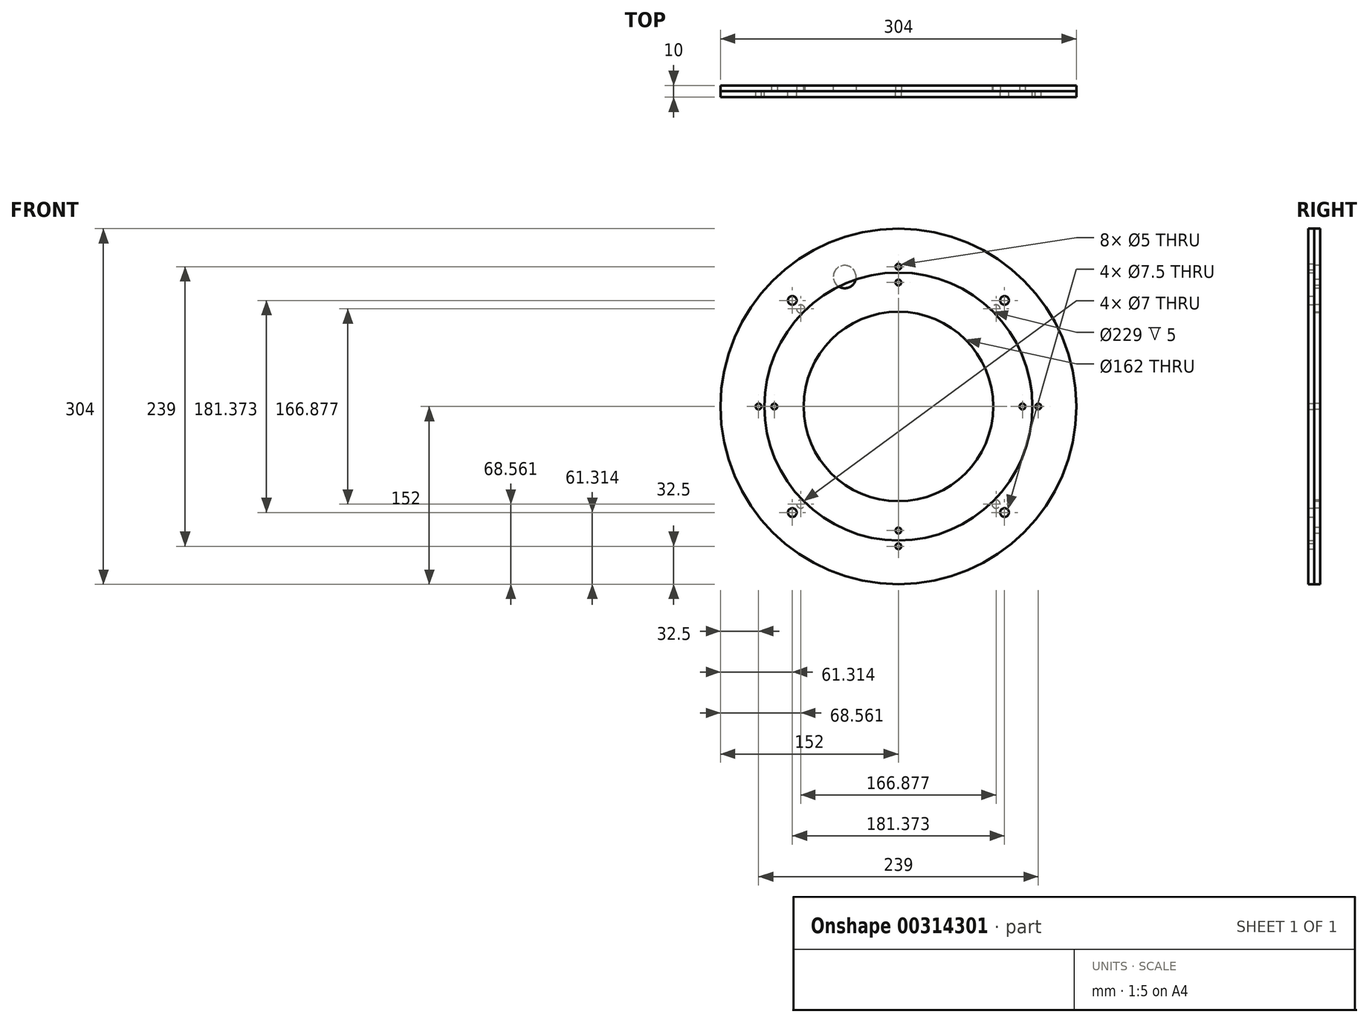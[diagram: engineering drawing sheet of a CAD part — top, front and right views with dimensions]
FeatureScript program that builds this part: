
annotation { "Feature Type Name" : "Feature", "Feature Type Description" : "" }
export const myFeature = defineFeature(function(context is Context, id is Id, definition is map)
    precondition{}
    {
        {
            var Q0;
            Q0=qCreatedBy(makeId("Front.planeOp"),FACE);
            var sketch = newSketch(context, id + "F0", { "sketchPlane" : qUnion([Q0])});
            skCircle(sketch, "E0", {"center": v(0, 0) * mm, "radius": 152 * mm});
            skCircle(sketch, "E1", {"center": v(0, 0) * mm, "radius": 81 * mm});
            skSolve(sketch);
        }
        {
            var Q0;
            Q0=makeQuery(id+"F0.imprint","IMPRINT",FACE,{"disambiguationData":[TD([[makeQuery(id+"F0.imprint","IMPRINT",EDGE,{"derivedFrom":sQuery(id+"F0.wireOp",EDGE,"E0")}),1.0]])]});
            extrude(context, id + "F1", {"entities" : qUnion([Q0]), "depth" : 5 * mm});
        }
        {
            var Q0;
            Q0=makeQuery(id+"F1.opExtrude","CAP_FACE",FACE,{"disambiguationData":[OSD([sQuery(id+"F0.wireOp",EDGE,"E0"),sQuery(id+"F0.wireOp",EDGE,"E1")])],"isStart":false});
            var sketch = newSketch(context, id + "F2", { "sketchPlane" : qUnion([Q0])});
            skCircle(sketch, "E2", {"center": v(0, 0) * mm, "radius": 106 * mm, "construction": true});
            skLineSegment(sketch, "E3", {"start": v(0, 0) * mm, "end": v(0, 106) * mm, "construction": true});
            skLineSegment(sketch, "E4", {"start": v(0, 0) * mm, "end": v(-106, 0) * mm, "construction": true});
            skLineSegment(sketch, "E5", {"start": v(0, 0) * mm, "end": v(0, -106) * mm, "construction": true});
            skLineSegment(sketch, "E6", {"start": v(0, 0) * mm, "end": v(106, 0) * mm, "construction": true});
            skCircle(sketch, "E7", {"center": v(0, 106) * mm, "radius": 2.5 * mm});
            skCircle(sketch, "E8", {"center": v(-106, 0) * mm, "radius": 2.5 * mm});
            skCircle(sketch, "E9", {"center": v(0, -106) * mm, "radius": 2.5 * mm});
            skCircle(sketch, "E10", {"center": v(106, 0) * mm, "radius": 2.5 * mm});
            skSolve(sketch);
        }
        {
            var Q0;
            Q0=makeQuery(id+"F2.imprint","IMPRINT",FACE,{"disambiguationData":[TD([[makeQuery(id+"F2.imprint","IMPRINT",EDGE,{"derivedFrom":sQuery(id+"F2.wireOp",EDGE,"E7")}),1.0]])]});
            extrude(context, id + "F3", {"entities" : qUnion([Q0]), "operationType" : NewBodyOperationType.REMOVE, "oppositeDirection" : true, "depth" : 5 * mm});
        }
        {
            var Q0;
            Q0=makeQuery(id+"F1.opExtrude","CAP_FACE",FACE,{"disambiguationData":[OSD([sQuery(id+"F0.wireOp",EDGE,"E0"),sQuery(id+"F0.wireOp",EDGE,"E1")])],"isStart":false});
            var sketch = newSketch(context, id + "F4", { "sketchPlane" : qUnion([Q0])});
            skSolve(sketch);
        }
        {
            var Q0;
            Q0 = qSketchRegion(id + "F4", true);
            var Q1;
            Q1=makeQuery(id+"F2.imprint","IMPRINT",FACE,{"disambiguationData":[TD([[makeQuery(id+"F2.imprint","IMPRINT",EDGE,{"derivedFrom":sQuery(id+"F2.wireOp",EDGE,"E8")}),1.0]])]});
            extrude(context, id + "F5", {"entities" : qUnion([Q0, Q1]), "operationType" : NewBodyOperationType.REMOVE, "oppositeDirection" : true, "depth" : 5 * mm});
        }
        {
            var Q0;
            Q0=makeQuery(id+"F2.imprint","IMPRINT",FACE,{"disambiguationData":[TD([[makeQuery(id+"F2.imprint","IMPRINT",EDGE,{"derivedFrom":sQuery(id+"F2.wireOp",EDGE,"E9")}),1.0]])]});
            extrude(context, id + "F6", {"entities" : qUnion([Q0]), "operationType" : NewBodyOperationType.REMOVE, "oppositeDirection" : true, "depth" : 5 * mm});
        }
        {
            var Q0;
            Q0=makeQuery(id+"F2.imprint","IMPRINT",FACE,{"disambiguationData":[TD([[makeQuery(id+"F2.imprint","IMPRINT",EDGE,{"derivedFrom":sQuery(id+"F2.wireOp",EDGE,"E10")}),1.0]])]});
            extrude(context, id + "F7", {"entities" : qUnion([Q0]), "operationType" : NewBodyOperationType.REMOVE, "oppositeDirection" : true, "depth" : 5 * mm});
        }
        {
            var Q0;
            Q0=makeQuery(id+"F4.imprint","IMPRINT",FACE,{"disambiguationData":[TD([[makeQuery(id+"F4.imprint","IMPRINT",EDGE,{"derivedFrom":makeQuery(id+"F1.opExtrude","CAP_EDGE",EDGE,{"disambiguationData":[OSD([sQuery(id+"F0.wireOp",EDGE,"E0")])],"isStart":false})}),1.0]])]});
            var sketch = newSketch(context, id + "F8", { "sketchPlane" : qUnion([Q0])});
            skLineSegment(sketch, "E11", {"start": v(0, 0) * mm, "end": v(83.44, 83.44) * mm, "construction": true});
            skCircle(sketch, "E12", {"center": v(0, 0) * mm, "radius": 118 * mm, "construction": true});
            skLineSegment(sketch, "E13", {"start": v(0, 0) * mm, "end": v(83.44, -83.44) * mm, "construction": true});
            skLineSegment(sketch, "E14", {"start": v(0, 0) * mm, "end": v(-83.44, 83.44) * mm, "construction": true});
            skLineSegment(sketch, "E15", {"start": v(0, 0) * mm, "end": v(-83.44, -83.44) * mm, "construction": true});
            skCircle(sketch, "E16", {"center": v(83.44, 83.44) * mm, "radius": 3.5 * mm});
            skCircle(sketch, "E17", {"center": v(83.44, -83.44) * mm, "radius": 3.5 * mm});
            skCircle(sketch, "E18", {"center": v(-83.44, -83.44) * mm, "radius": 3.5 * mm});
            skCircle(sketch, "E19", {"center": v(-83.44, 83.44) * mm, "radius": 3.5 * mm});
            skLineSegment(sketch, "E20", {"start": v(0, 0) * mm, "end": v(-45.92, 110.87) * mm, "construction": true});
            skCircle(sketch, "E21", {"center": v(-45.92, 110.87) * mm, "radius": 9.75 * mm});
            skSolve(sketch);
        }
        {
            var Q0;
            Q0 = qSketchRegion(id + "F8", true);
            var Q1;
            Q1=makeQuery(id+"F1.opExtrude","CAP_FACE",FACE,{"disambiguationData":[OSD([sQuery(id+"F0.wireOp",EDGE,"E0"),sQuery(id+"F0.wireOp",EDGE,"E1")])],"isStart":true});
            extrude(context, id + "F9", {"entities" : qUnion([Q0]), "operationType" : NewBodyOperationType.REMOVE, "endBound" : BoundingType.UP_TO_SURFACE, "oppositeDirection" : true, "endBoundEntityFace" : qUnion([Q1]), "depth" : 5 * mm});
        }
        {
            var Q0;
            Q0=makeQuery(id+"F2.imprint","IMPRINT",FACE,{"disambiguationData":[TD([[makeQuery(id+"F2.imprint","IMPRINT",EDGE,{"derivedFrom":sQuery(id+"F2.wireOp",EDGE,"E7")}),-1.0]])]});
            var sketch = newSketch(context, id + "F10", { "sketchPlane" : qUnion([Q0])});
            skCircle(sketch, "E22", {"center": v(0, 0) * mm, "radius": 152 * mm});
            skCircle(sketch, "E23", {"center": v(0, 0) * mm, "radius": 114.5 * mm});
            skCircle(sketch, "E24", {"center": v(0, 0) * mm, "radius": 119.5 * mm, "construction": true});
            skLineSegment(sketch, "E25", {"start": v(0, 0) * mm, "end": v(0, 119.5) * mm, "construction": true});
            skLineSegment(sketch, "E26", {"start": v(0, 0) * mm, "end": v(0, -119.5) * mm, "construction": true});
            skLineSegment(sketch, "E27", {"start": v(0, 0) * mm, "end": v(-119.5, 0) * mm, "construction": true});
            skLineSegment(sketch, "E28", {"start": v(0, 0) * mm, "end": v(119.5, 0) * mm, "construction": true});
            skCircle(sketch, "E29", {"center": v(0, 119.5) * mm, "radius": 2.5 * mm});
            skCircle(sketch, "E30", {"center": v(-119.5, 0) * mm, "radius": 2.5 * mm});
            skCircle(sketch, "E31", {"center": v(0, -119.5) * mm, "radius": 2.5 * mm});
            skCircle(sketch, "E32", {"center": v(119.5, 0) * mm, "radius": 2.5 * mm});
            skCircle(sketch, "E33", {"center": v(0, 0) * mm, "radius": 128.25 * mm, "construction": true});
            skLineSegment(sketch, "E34", {"start": v(0, 0) * mm, "end": v(-90.69, 90.69) * mm, "construction": true});
            skLineSegment(sketch, "E35", {"start": v(0, 0) * mm, "end": v(-90.69, -90.69) * mm, "construction": true});
            skLineSegment(sketch, "E36", {"start": v(0, 0) * mm, "end": v(90.69, 90.69) * mm, "construction": true});
            skLineSegment(sketch, "E37", {"start": v(0, 0) * mm, "end": v(90.69, -90.69) * mm, "construction": true});
            skCircle(sketch, "E38", {"center": v(-90.69, 90.69) * mm, "radius": 3.75 * mm});
            skCircle(sketch, "E39", {"center": v(-90.69, -90.69) * mm, "radius": 3.75 * mm});
            skCircle(sketch, "E40", {"center": v(90.69, -90.69) * mm, "radius": 3.75 * mm});
            skCircle(sketch, "E41", {"center": v(90.69, 90.69) * mm, "radius": 3.75 * mm});
            skSolve(sketch);
        }
        {
            var Q0;
            Q0 = qSketchRegion(id + "F10", true);
            extrude(context, id + "F11", {"entities" : qUnion([Q0]), "depth" : 5 * mm});
        }
    });
